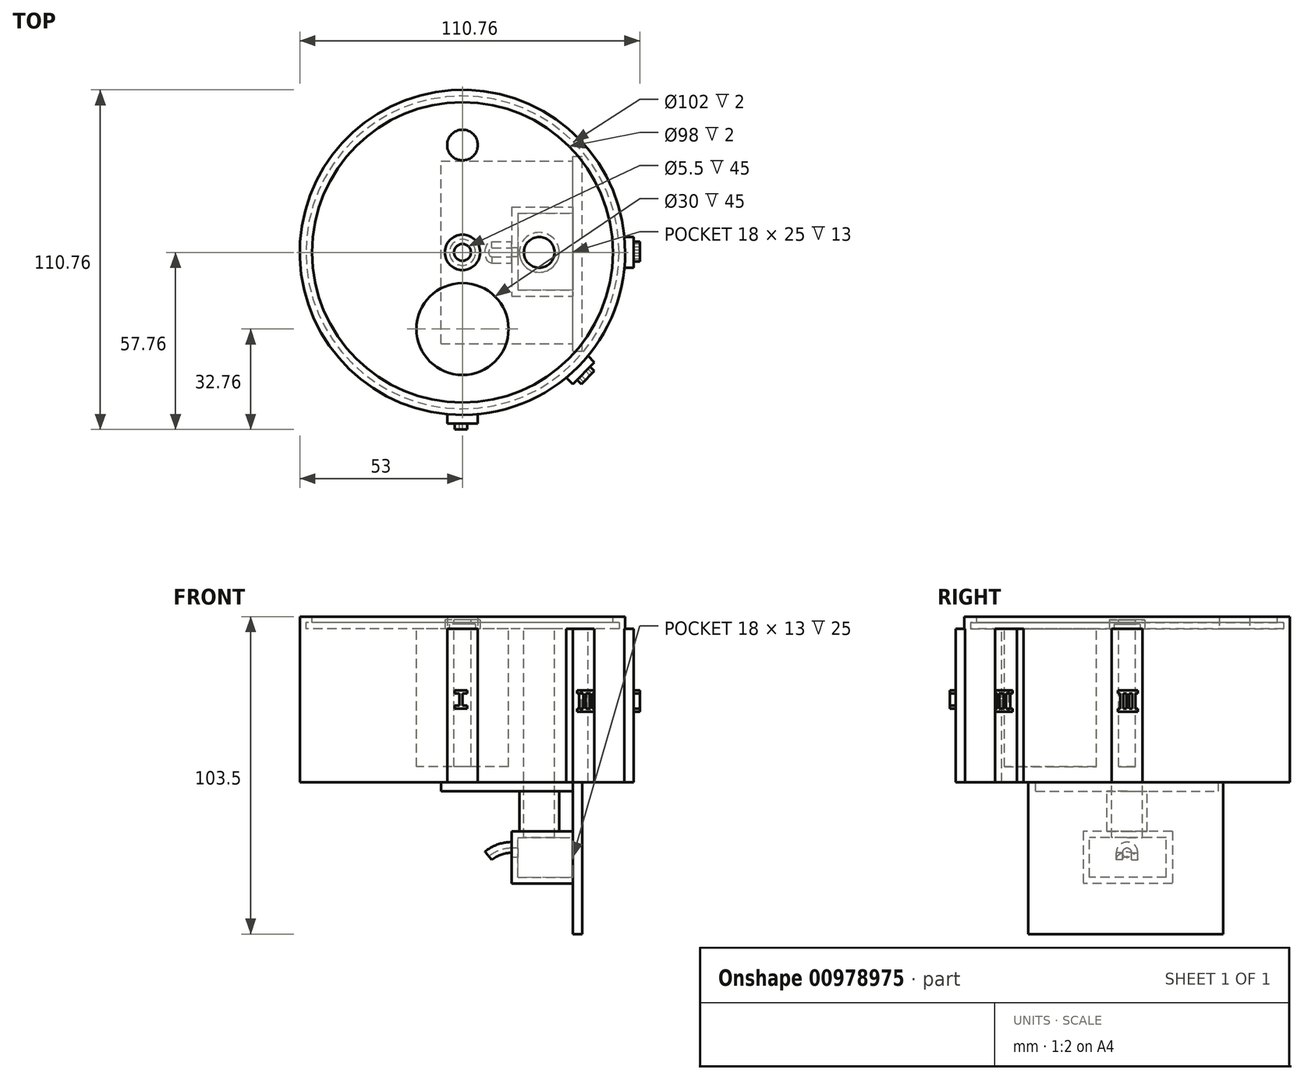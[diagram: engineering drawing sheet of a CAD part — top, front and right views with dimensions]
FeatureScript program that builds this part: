
annotation { "Feature Type Name" : "Feature", "Feature Type Description" : "" }
export const myFeature = defineFeature(function(context is Context, id is Id, definition is map)
    precondition{}
    {
        {
            var Q0;
            Q0=qCreatedBy(makeId("Top.planeOp"),FACE);
            var sketch = newSketch(context, id + "F0", { "sketchPlane" : qUnion([Q0])});
            skCircle(sketch, "E0", {"center": v(0, 0) * mm, "radius": 53 * mm});
            skSolve(sketch);
        }
        {
            var Q0;
            Q0=makeQuery(id+"F0.imprint","IMPRINT",FACE,{"disambiguationData":[TD([[makeQuery(id+"F0.imprint","IMPRINT",EDGE,{"derivedFrom":sQuery(id+"F0.wireOp",EDGE,"E0")}),1.0]])]});
            extrude(context, id + "F1", {"entities" : qUnion([Q0]), "depth" : 50 * mm, "offsetDistance" : 25 * mm});
        }
        {
            var Q0;
            Q0=makeQuery(id+"F1.opExtrude","CAP_FACE",FACE,{"disambiguationData":[OSD([sQuery(id+"F0.wireOp",EDGE,"E0")])],"isStart":false});
            var sketch = newSketch(context, id + "F2", { "sketchPlane" : qUnion([Q0])});
            skCircle(sketch, "E1", {"center": v(0, 0) * mm, "radius": 5.75 * mm});
            skCircle(sketch, "E2", {"center": v(0, 0) * mm, "radius": 51 * mm});
            skCircle(sketch, "E3", {"center": v(0, 0) * mm, "radius": 4.25 * mm});
            skCircle(sketch, "E4", {"center": v(0, 0) * mm, "radius": 2.75 * mm});
            skCircle(sketch, "E5", {"center": v(0, 35) * mm, "radius": 5 * mm});
            skCircle(sketch, "E6", {"center": v(0, -25) * mm, "radius": 15 * mm});
            skCircle(sketch, "E7", {"center": v(25, 0) * mm, "radius": 5 * mm});
            skLineSegment(sketch, "E8", {"start": v(-5, -52.76) * mm, "end": v(-5, -55.76) * mm});
            skLineSegment(sketch, "E9", {"start": v(-5, -55.76) * mm, "end": v(5, -55.76) * mm});
            skLineSegment(sketch, "E10", {"start": v(5, -55.76) * mm, "end": v(5, -52.76) * mm});
            skLineSegment(sketch, "E11", {"start": v(52.76, -5) * mm, "end": v(55.76, -5) * mm});
            skLineSegment(sketch, "E12", {"start": v(55.76, -5) * mm, "end": v(55.76, 5) * mm});
            skLineSegment(sketch, "E13", {"start": v(55.76, 5) * mm, "end": v(52.76, 5) * mm});
            skLineSegment(sketch, "E14", {"start": v(33.77, -40.85) * mm, "end": v(35.9, -42.97) * mm});
            skLineSegment(sketch, "E15", {"start": v(35.9, -42.97) * mm, "end": v(42.97, -35.9) * mm});
            skLineSegment(sketch, "E16", {"start": v(42.97, -35.9) * mm, "end": v(40.85, -33.77) * mm});
            skSolve(sketch);
        }
        {
            var Q0;
            Q0=makeQuery(id+"F2.imprint","IMPRINT",FACE,{"disambiguationData":[TD([[makeQuery(id+"F2.imprint","IMPRINT",EDGE,{"derivedFrom":sQuery(id+"F2.wireOp",EDGE,"E1")}),1.0]])]});
            extrude(context, id + "F3", {"entities" : qUnion([Q0]), "operationType" : NewBodyOperationType.ADD, "depth" : 3 * mm, "offsetDistance" : 25 * mm});
        }
        {
            var Q0;
            Q0=makeQuery(id+"F2.imprint","IMPRINT",FACE,{"disambiguationData":[TD([[makeQuery(id+"F2.imprint","IMPRINT",EDGE,{"derivedFrom":sQuery(id+"F2.wireOp",EDGE,"E2")}),-1.0]])]});
            extrude(context, id + "F4", {"entities" : qUnion([Q0]), "operationType" : NewBodyOperationType.ADD, "depth" : 4 * mm, "offsetDistance" : 25 * mm});
        }
        {
            var Q0;
            Q0=makeQuery(id+"F2.imprint","IMPRINT",FACE,{"disambiguationData":[TD([[makeQuery(id+"F2.imprint","IMPRINT",EDGE,{"derivedFrom":sQuery(id+"F2.wireOp",EDGE,"E4")}),1.0]])]});
            extrude(context, id + "F5", {"entities" : qUnion([Q0]), "operationType" : NewBodyOperationType.REMOVE, "oppositeDirection" : true, "depth" : 45 * mm, "offsetDistance" : 25 * mm});
        }
        {
            var Q0;
            Q0=makeQuery(id+"F4.opExtrude","CAP_FACE",FACE,{"disambiguationData":[OSD([sQuery(id+"F0.wireOp",EDGE,"E0"),sQuery(id+"F2.wireOp",EDGE,"E2")])],"isStart":false});
            var sketch = newSketch(context, id + "F6", { "sketchPlane" : qUnion([Q0])});
            skCircle(sketch, "E17", {"center": v(0, 0) * mm, "radius": 49 * mm});
            skSolve(sketch);
        }
        {
            var Q0;
            Q0=makeQuery(id+"F6.imprint","IMPRINT",FACE,{"disambiguationData":[TD([[makeQuery(id+"F6.imprint","IMPRINT",EDGE,{"derivedFrom":sQuery(id+"F6.wireOp",EDGE,"E17")}),-1.0]])]});
            extrude(context, id + "F7", {"entities" : qUnion([Q0]), "operationType" : NewBodyOperationType.ADD, "oppositeDirection" : true, "depth" : 2 * mm, "offsetDistance" : 25 * mm});
        }
        {
            var Q0;
            Q0=makeQuery(id+"F3.opExtrude","CAP_FACE",FACE,{"disambiguationData":[OSD([sQuery(id+"F2.wireOp",EDGE,"E1"),sQuery(id+"F2.wireOp",EDGE,"E3")])],"isStart":false});
            var sketch = newSketch(context, id + "F8", { "sketchPlane" : qUnion([Q0])});
            skCircle(sketch, "E18", {"center": v(0, 0) * mm, "radius": 2.75 * mm});
            skSolve(sketch);
        }
        {
            var Q0;
            Q0=makeQuery(id+"F8.imprint","IMPRINT",FACE,{"disambiguationData":[TD([[makeQuery(id+"F8.imprint","IMPRINT",EDGE,{"derivedFrom":sQuery(id+"F8.wireOp",EDGE,"E18")}),-1.0]])]});
            extrude(context, id + "F9", {"entities" : qUnion([Q0]), "operationType" : NewBodyOperationType.ADD, "oppositeDirection" : true, "depth" : 1.5 * mm, "offsetDistance" : 25 * mm});
        }
        {
            var Q0;
            Q0=makeQuery(id+"F2.imprint","IMPRINT",FACE,{"disambiguationData":[TD([[makeQuery(id+"F2.imprint","IMPRINT",EDGE,{"derivedFrom":sQuery(id+"F2.wireOp",EDGE,"E5")}),1.0]])]});
            extrude(context, id + "F10", {"entities" : qUnion([Q0]), "operationType" : NewBodyOperationType.ADD, "depth" : 4 * mm, "offsetDistance" : 25 * mm});
        }
        {
            var Q0;
            Q0=makeQuery(id+"F2.imprint","IMPRINT",FACE,{"disambiguationData":[TD([[makeQuery(id+"F2.imprint","IMPRINT",EDGE,{"derivedFrom":sQuery(id+"F2.wireOp",EDGE,"E7")}),1.0]])]});
            extrude(context, id + "F11", {"entities" : qUnion([Q0]), "operationType" : NewBodyOperationType.REMOVE, "oppositeDirection" : true, "depth" : 150 * mm, "offsetDistance" : 25 * mm});
        }
        {
            var Q0;
            Q0=makeQuery(id+"F2.imprint","IMPRINT",FACE,{"disambiguationData":[TD([[makeQuery(id+"F2.imprint","IMPRINT",EDGE,{"derivedFrom":sQuery(id+"F2.wireOp",EDGE,"E6")}),1.0]])]});
            extrude(context, id + "F12", {"entities" : qUnion([Q0]), "operationType" : NewBodyOperationType.REMOVE, "oppositeDirection" : true, "depth" : 45 * mm, "offsetDistance" : 25 * mm});
        }
        {
            var Q0;
            {var subQ0=sQuery(id+"F2.wireOp",EDGE,"E11");Q0=makeQuery(id+"F2.imprint","IMPRINT",FACE,{"disambiguationData":[TD([[makeQuery(id+"F2.imprint","IMPRINT",EDGE,{"derivedFrom":subQ0}),1.0]])]});}
            var Q1;
            {var subQ0=sQuery(id+"F2.wireOp",EDGE,"E8");Q1=makeQuery(id+"F2.imprint","IMPRINT",FACE,{"disambiguationData":[TD([[makeQuery(id+"F2.imprint","IMPRINT",EDGE,{"derivedFrom":subQ0}),1.0]])]});}
            var Q2;
            {var subQ0=sQuery(id+"F2.wireOp",EDGE,"E14");Q2=makeQuery(id+"F2.imprint","IMPRINT",FACE,{"disambiguationData":[TD([[makeQuery(id+"F2.imprint","IMPRINT",EDGE,{"derivedFrom":subQ0}),1.0]])]});}
            extrude(context, id + "F13", {"entities" : qUnion([Q0, Q1, Q2]), "operationType" : NewBodyOperationType.ADD, "oppositeDirection" : true, "depth" : 50 * mm, "offsetDistance" : 25 * mm});
        }
        {
            var Q0;
            {var subQ0=sQuery(id+"F0.wireOp",EDGE,"E0");Q0=makeQuery(id+"F13.boolean.opBoolean","MERGE",FACE,{"derivedFrom":[makeQuery(id+"F1.opExtrude","CAP_FACE",FACE,{"disambiguationData":[OSD([subQ0])],"isStart":true}),makeQuery(id+"F13.opExtrude","CAP_FACE",FACE,{"disambiguationData":[OSD([subQ0,sQuery(id+"F2.wireOp",EDGE,"E8"),sQuery(id+"F2.wireOp",EDGE,"E9"),sQuery(id+"F2.wireOp",EDGE,"E10")])],"isStart":false}),makeQuery(id+"F13.opExtrude","CAP_FACE",FACE,{"disambiguationData":[OSD([subQ0,sQuery(id+"F2.wireOp",EDGE,"E11"),sQuery(id+"F2.wireOp",EDGE,"E12"),sQuery(id+"F2.wireOp",EDGE,"E13")])],"isStart":false}),makeQuery(id+"F13.opExtrude","CAP_FACE",FACE,{"disambiguationData":[OSD([subQ0,sQuery(id+"F2.wireOp",EDGE,"E14"),sQuery(id+"F2.wireOp",EDGE,"E15"),sQuery(id+"F2.wireOp",EDGE,"E16")])],"isStart":false})]});}
            var sketch = newSketch(context, id + "F14", { "sketchPlane" : qUnion([Q0])});
            skLineSegment(sketch, "E19.bottom", {"start": v(-7, 29.75) * mm, "end": v(36, 29.75) * mm});
            skLineSegment(sketch, "E19.top", {"start": v(-7, -29.75) * mm, "end": v(36, -29.75) * mm});
            skLineSegment(sketch, "E19.left", {"start": v(-7, 29.75) * mm, "end": v(-7, -29.75) * mm});
            skLineSegment(sketch, "E19.right", {"start": v(36, 29.75) * mm, "end": v(36, -29.75) * mm});
            skLineSegment(sketch, "E20.bottom", {"start": v(36, 32.25) * mm, "end": v(39, 32.25) * mm});
            skLineSegment(sketch, "E20.top", {"start": v(36, -31.25) * mm, "end": v(39, -31.25) * mm});
            skLineSegment(sketch, "E20.left", {"start": v(36, 32.25) * mm, "end": v(36, -31.25) * mm});
            skLineSegment(sketch, "E20.right", {"start": v(39, 32.25) * mm, "end": v(39, -31.25) * mm});
            skSolve(sketch);
        }
        {
            var Q0;
            Q0=makeQuery(id+"F14.imprint","IMPRINT",FACE,{"disambiguationData":[TD([[makeQuery(id+"F14.imprint","IMPRINT",EDGE,{"derivedFrom":sQuery(id+"F14.wireOp",EDGE,"E19.bottom")}),-1.0]])]});
            extrude(context, id + "F15", {"entities" : qUnion([Q0]), "operationType" : NewBodyOperationType.ADD, "depth" : 3 * mm, "offsetDistance" : 25 * mm});
        }
        {
            var Q0;
            {var subQ1=sQuery(id+"F14.wireOp",EDGE,"E19.right");Q0=makeQuery(id+"F14.imprint","IMPRINT",FACE,{"disambiguationData":[TD([[makeQuery(id+"F14.imprint","IMPRINT",EDGE,{"derivedFrom":subQ1}),1.0]])]});}
            extrude(context, id + "F16", {"entities" : qUnion([Q0]), "operationType" : NewBodyOperationType.ADD, "depth" : 49.5 * mm, "offsetDistance" : 25 * mm});
        }
        {
            var Q0;
            Q0=makeQuery(id+"F15.opExtrude","CAP_FACE",FACE,{"disambiguationData":[OSD([sQuery(id+"F0.wireOp",EDGE,"E0"),sQuery(id+"F2.wireOp",EDGE,"E7"),sQuery(id+"F14.wireOp",EDGE,"E19.bottom"),sQuery(id+"F14.wireOp",EDGE,"E19.top"),sQuery(id+"F14.wireOp",EDGE,"E19.left"),sQuery(id+"F14.wireOp",EDGE,"E19.right")])],"isStart":false});
            var sketch = newSketch(context, id + "F17", { "sketchPlane" : qUnion([Q0])});
            skCircle(sketch, "E21", {"center": v(25, 0) * mm, "radius": 6.5 * mm});
            skSolve(sketch);
        }
        {
            var Q0;
            Q0=makeQuery(id+"F17.imprint","IMPRINT",FACE,{"disambiguationData":[TD([[makeQuery(id+"F17.imprint","IMPRINT",EDGE,{"derivedFrom":sQuery(id+"F17.wireOp",EDGE,"E21")}),1.0]])]});
            extrude(context, id + "F18", {"entities" : qUnion([Q0]), "operationType" : NewBodyOperationType.ADD, "depth" : 15 * mm, "offsetDistance" : 25 * mm});
        }
        {
            var Q0;
            Q0=makeQuery(id+"F16.opExtrude","SWEPT_FACE",FACE,{"disambiguationData":[OSD([sQuery(id+"F14.wireOp",EDGE,"E19.right"),sQuery(id+"F14.wireOp",EDGE,"E20.left")])]});
            var sketch = newSketch(context, id + "F19", { "sketchPlane" : qUnion([Q0])});
            skLineSegment(sketch, "E22.bottom", {"start": v(-14.75, -16) * mm, "end": v(14.25, -16) * mm});
            skLineSegment(sketch, "E22.top", {"start": v(-14.75, -33) * mm, "end": v(14.25, -33) * mm});
            skLineSegment(sketch, "E22.left", {"start": v(-14.75, -16) * mm, "end": v(-14.75, -33) * mm});
            skLineSegment(sketch, "E22.right", {"start": v(14.25, -16) * mm, "end": v(14.25, -33) * mm});
            skLineSegment(sketch, "E23.bottom", {"start": v(-12.75, -31) * mm, "end": v(12.25, -31) * mm});
            skLineSegment(sketch, "E23.top", {"start": v(-12.75, -18) * mm, "end": v(12.25, -18) * mm});
            skLineSegment(sketch, "E23.left", {"start": v(-12.75, -31) * mm, "end": v(-12.75, -18) * mm});
            skLineSegment(sketch, "E23.right", {"start": v(12.25, -31) * mm, "end": v(12.25, -18) * mm});
            skSolve(sketch);
        }
        {
            var Q0;
            Q0=makeQuery(id+"F19.imprint","IMPRINT",FACE,{"disambiguationData":[TD([[makeQuery(id+"F19.imprint","IMPRINT",EDGE,{"derivedFrom":sQuery(id+"F19.wireOp",EDGE,"E22.bottom")}),-1.0]])]});
            extrude(context, id + "F20", {"entities" : qUnion([Q0]), "operationType" : NewBodyOperationType.ADD, "depth" : 20 * mm, "offsetDistance" : 25 * mm});
        }
        {
            var Q0;
            Q0=makeQuery(id+"F20.boolean.opBoolean","MERGE",FACE,{"derivedFrom":[makeQuery(id+"F18.opExtrude","CAP_FACE",FACE,{"disambiguationData":[OSD([sQuery(id+"F0.wireOp",EDGE,"E0"),sQuery(id+"F2.wireOp",EDGE,"E7"),sQuery(id+"F17.wireOp",EDGE,"E21")])],"isStart":false}),makeQuery(id+"F20.opExtrude","SWEPT_FACE",FACE,{"disambiguationData":[OSD([sQuery(id+"F19.wireOp",EDGE,"E23.top")])]})]});
            var sketch = newSketch(context, id + "F21", { "sketchPlane" : qUnion([Q0])});
            skCircle(sketch, "E24", {"center": v(25, 0) * mm, "radius": 5 * mm});
            skSolve(sketch);
        }
        {
            var Q0;
            Q0=makeQuery(id+"F21.imprint","IMPRINT",FACE,{"disambiguationData":[TD([[makeQuery(id+"F21.imprint","IMPRINT",EDGE,{"derivedFrom":sQuery(id+"F21.wireOp",EDGE,"E24")}),1.0]])]});
            extrude(context, id + "F22", {"entities" : qUnion([Q0]), "operationType" : NewBodyOperationType.REMOVE, "oppositeDirection" : true, "depth" : 25 * mm, "offsetDistance" : 25 * mm});
        }
        {
            var Q0;
            Q0=makeQuery(id+"F20.opExtrude","CAP_FACE",FACE,{"disambiguationData":[OSD([sQuery(id+"F19.wireOp",EDGE,"E22.bottom"),sQuery(id+"F19.wireOp",EDGE,"E22.top"),sQuery(id+"F19.wireOp",EDGE,"E22.left"),sQuery(id+"F19.wireOp",EDGE,"E22.right"),sQuery(id+"F19.wireOp",EDGE,"E23.bottom"),sQuery(id+"F19.wireOp",EDGE,"E23.top"),sQuery(id+"F19.wireOp",EDGE,"E23.left"),sQuery(id+"F19.wireOp",EDGE,"E23.right")])],"isStart":false});
            var sketch = newSketch(context, id + "F23", { "sketchPlane" : qUnion([Q0])});
            skCircle(sketch, "E25", {"center": v(0, -23) * mm, "radius": 1.5 * mm});
            skCircle(sketch, "E26", {"center": v(0, -23) * mm, "radius": 3.5 * mm});
            skLineSegment(sketch, "E27", {"start": v(0, -23) * mm, "end": v(-3.5, -23) * mm});
            skLineSegment(sketch, "E28", {"start": v(-3.5, -23) * mm, "end": v(3.5, -23) * mm});
            skSolve(sketch);
        }
        {
            var Q0;
            Q0=makeQuery(id+"F23.imprint","IMPRINT",FACE,{"disambiguationData":[TD([[makeQuery(id+"F23.imprint","IMPRINT",EDGE,{"derivedFrom":makeQuery(id+"F20.opExtrude","CAP_EDGE",EDGE,{"disambiguationData":[OSD([sQuery(id+"F19.wireOp",EDGE,"E23.bottom")])],"isStart":false})}),1.0]])]});
            var Q1;
            {var subQ0=sQuery(id+"F23.wireOp",EDGE,"E27");var subQ1=sQuery(id+"F23.wireOp",EDGE,"E25");var subQ2=makeQuery(id+"F23.imprint","INTERSECT",VERTEX,{"derivedFrom":[subQ1,subQ0]});Q1=makeQuery(id+"F23.imprint","IMPRINT",FACE,{"disambiguationData":[TD([[makeQuery(id+"F23.imprint","IMPRINT",EDGE,{"disambiguationData":[TD([[subQ2,-1.0]])],"derivedFrom":subQ1}),-1.0]])]});}
            var Q2;
            {var subQ0=sQuery(id+"F23.wireOp",EDGE,"E27");var subQ1=sQuery(id+"F23.wireOp",EDGE,"E25");var subQ2=makeQuery(id+"F23.imprint","INTERSECT",VERTEX,{"derivedFrom":[subQ1,subQ0]});Q2=makeQuery(id+"F23.imprint","IMPRINT",FACE,{"disambiguationData":[TD([[makeQuery(id+"F23.imprint","IMPRINT",EDGE,{"disambiguationData":[TD([[subQ2,1.0]])],"derivedFrom":subQ1}),-1.0]])]});}
            extrude(context, id + "F24", {"entities" : qUnion([Q0, Q1, Q2]), "operationType" : NewBodyOperationType.ADD, "oppositeDirection" : true, "depth" : 2 * mm, "offsetDistance" : 25 * mm});
        }
        {
            var Q0;
            {var subQ0=sQuery(id+"F23.wireOp",EDGE,"E27");var subQ1=sQuery(id+"F23.wireOp",EDGE,"E25");var subQ2=makeQuery(id+"F23.imprint","INTERSECT",VERTEX,{"derivedFrom":[subQ1,subQ0]});Q0=makeQuery(id+"F23.imprint","IMPRINT",FACE,{"disambiguationData":[TD([[makeQuery(id+"F23.imprint","IMPRINT",EDGE,{"disambiguationData":[TD([[subQ2,1.0]])],"derivedFrom":subQ1}),-1.0]])]});}
            var Q1;
            Q1=makeQuery(id+"F20.opExtrude","CAP_EDGE",EDGE,{"disambiguationData":[OSD([sQuery(id+"F19.wireOp",EDGE,"E22.top")])],"isStart":false});
            revolve(context, id + "F25", {"operationType" : NewBodyOperationType.ADD, "surfaceOperationType" : NewSurfaceOperationType.NEW, "entities" : qUnion([Q0]), "axis" : qUnion([Q1]), "revolveType" : RevolveType.ONE_DIRECTION, "angle" : 40 * degree});
        }
        {
            var Q0;
            Q0=makeQuery(id+"F13.opExtrude","SWEPT_FACE",FACE,{"disambiguationData":[OSD([sQuery(id+"F2.wireOp",EDGE,"E9")])]});
            var sketch = newSketch(context, id + "F26", { "sketchPlane" : qUnion([Q0])});
            skLineSegment(sketch, "E29", {"start": v(-2.5, 30) * mm, "end": v(1.5, 30) * mm});
            skLineSegment(sketch, "E30", {"start": v(1.5, 30) * mm, "end": v(1.5, 29) * mm});
            skLineSegment(sketch, "E31", {"start": v(1.5, 29) * mm, "end": v(0, 29) * mm});
            skLineSegment(sketch, "E32", {"start": v(0, 29) * mm, "end": v(0, 25) * mm});
            skLineSegment(sketch, "E33", {"start": v(0, 25) * mm, "end": v(1.5, 25) * mm});
            skLineSegment(sketch, "E34", {"start": v(1.5, 25) * mm, "end": v(1.5, 24) * mm});
            skLineSegment(sketch, "E35", {"start": v(1.5, 24) * mm, "end": v(-2.5, 24) * mm});
            skLineSegment(sketch, "E36", {"start": v(-2.5, 24) * mm, "end": v(-2.5, 25) * mm});
            skLineSegment(sketch, "E37", {"start": v(-2.5, 25) * mm, "end": v(-1, 25) * mm});
            skLineSegment(sketch, "E38", {"start": v(-1, 25) * mm, "end": v(-1, 29) * mm});
            skLineSegment(sketch, "E39", {"start": v(-1, 29) * mm, "end": v(-2.5, 29) * mm});
            skLineSegment(sketch, "E40", {"start": v(-2.5, 29) * mm, "end": v(-2.5, 30) * mm});
            skSolve(sketch);
        }
        {
            var Q0;
            Q0=makeQuery(id+"F26.imprint","IMPRINT",FACE,{"disambiguationData":[TD([[makeQuery(id+"F26.imprint","IMPRINT",EDGE,{"derivedFrom":sQuery(id+"F26.wireOp",EDGE,"E29")}),-1.0]])]});
            extrude(context, id + "F27", {"entities" : qUnion([Q0]), "operationType" : NewBodyOperationType.ADD, "depth" : 2 * mm, "offsetDistance" : 25 * mm});
        }
        {
            var Q0;
            Q0=makeQuery(id+"F13.opExtrude","SWEPT_FACE",FACE,{"disambiguationData":[OSD([sQuery(id+"F2.wireOp",EDGE,"E15")])]});
            var sketch = newSketch(context, id + "F28", { "sketchPlane" : qUnion([Q0])});
            skLineSegment(sketch, "E41", {"start": v(-3, 30) * mm, "end": v(3, 30) * mm});
            skLineSegment(sketch, "E42", {"start": v(3, 30) * mm, "end": v(3, 29) * mm});
            skLineSegment(sketch, "E43", {"start": v(3, 29) * mm, "end": v(2, 29) * mm});
            skLineSegment(sketch, "E44", {"start": v(2, 29) * mm, "end": v(2, 24) * mm});
            skLineSegment(sketch, "E45", {"start": v(2, 24) * mm, "end": v(3, 24) * mm});
            skLineSegment(sketch, "E46", {"start": v(3, 24) * mm, "end": v(3, 23) * mm});
            skLineSegment(sketch, "E47", {"start": v(3, 23) * mm, "end": v(-3, 23) * mm});
            skLineSegment(sketch, "E48", {"start": v(-3, 23) * mm, "end": v(-3, 24) * mm});
            skLineSegment(sketch, "E49", {"start": v(-3, 24) * mm, "end": v(-2, 24) * mm});
            skLineSegment(sketch, "E50", {"start": v(-2, 24) * mm, "end": v(-2, 29) * mm});
            skLineSegment(sketch, "E51", {"start": v(-2, 29) * mm, "end": v(-3, 29) * mm});
            skLineSegment(sketch, "E52", {"start": v(-3, 29) * mm, "end": v(-3, 30) * mm});
            skLineSegment(sketch, "E53", {"start": v(-1, 29) * mm, "end": v(1, 29) * mm});
            skLineSegment(sketch, "E54", {"start": v(1, 29) * mm, "end": v(1, 24) * mm});
            skLineSegment(sketch, "E55", {"start": v(1, 24) * mm, "end": v(-1, 24) * mm});
            skLineSegment(sketch, "E56", {"start": v(-1, 24) * mm, "end": v(-1, 29) * mm});
            skSolve(sketch);
        }
        {
            var Q0;
            Q0=makeQuery(id+"F28.imprint","IMPRINT",FACE,{"disambiguationData":[TD([[makeQuery(id+"F28.imprint","IMPRINT",EDGE,{"derivedFrom":sQuery(id+"F28.wireOp",EDGE,"E41")}),-1.0]])]});
            extrude(context, id + "F29", {"entities" : qUnion([Q0]), "operationType" : NewBodyOperationType.ADD, "depth" : 2 * mm, "offsetDistance" : 25 * mm});
        }
        {
            var Q0;
            Q0=makeQuery(id+"F13.opExtrude","SWEPT_FACE",FACE,{"disambiguationData":[OSD([sQuery(id+"F2.wireOp",EDGE,"E12")])]});
            var sketch = newSketch(context, id + "F30", { "sketchPlane" : qUnion([Q0])});
            skLineSegment(sketch, "E57", {"start": v(-3, 30) * mm, "end": v(3.5, 30) * mm});
            skLineSegment(sketch, "E58", {"start": v(3.5, 30) * mm, "end": v(3.5, 29) * mm});
            skLineSegment(sketch, "E59", {"start": v(3.5, 29) * mm, "end": v(2.75, 29) * mm});
            skLineSegment(sketch, "E60", {"start": v(2.75, 29) * mm, "end": v(2.75, 24) * mm});
            skLineSegment(sketch, "E61", {"start": v(2.75, 24) * mm, "end": v(3.5, 24) * mm});
            skLineSegment(sketch, "E62", {"start": v(3.5, 24) * mm, "end": v(3.5, 23) * mm});
            skLineSegment(sketch, "E63", {"start": v(3.5, 23) * mm, "end": v(-3, 23) * mm});
            skLineSegment(sketch, "E64", {"start": v(-3, 23) * mm, "end": v(-3, 24) * mm});
            skLineSegment(sketch, "E65", {"start": v(-3, 24) * mm, "end": v(-2.25, 24) * mm});
            skLineSegment(sketch, "E66", {"start": v(-2.25, 24) * mm, "end": v(-2.25, 29) * mm});
            skLineSegment(sketch, "E67", {"start": v(-2.25, 29) * mm, "end": v(-3, 29) * mm});
            skLineSegment(sketch, "E68", {"start": v(-3, 29) * mm, "end": v(-3, 30) * mm});
            skLineSegment(sketch, "E69", {"start": v(-1.25, 24) * mm, "end": v(-1.25, 29) * mm});
            skLineSegment(sketch, "E70", {"start": v(-1.25, 29) * mm, "end": v(-0.25, 29) * mm});
            skLineSegment(sketch, "E71", {"start": v(-0.25, 29) * mm, "end": v(-0.25, 24) * mm});
            skLineSegment(sketch, "E72", {"start": v(-0.25, 24) * mm, "end": v(-1.25, 24) * mm});
            skLineSegment(sketch, "E73", {"start": v(0.75, 24) * mm, "end": v(0.75, 29) * mm});
            skLineSegment(sketch, "E74", {"start": v(0.75, 29) * mm, "end": v(1.75, 29) * mm});
            skLineSegment(sketch, "E75", {"start": v(1.75, 29) * mm, "end": v(1.75, 24) * mm});
            skLineSegment(sketch, "E76", {"start": v(1.75, 24) * mm, "end": v(0.75, 24) * mm});
            skSolve(sketch);
        }
        {
            var Q0;
            Q0=makeQuery(id+"F30.imprint","IMPRINT",FACE,{"disambiguationData":[TD([[makeQuery(id+"F30.imprint","IMPRINT",EDGE,{"derivedFrom":sQuery(id+"F30.wireOp",EDGE,"E57")}),-1.0]])]});
            extrude(context, id + "F31", {"entities" : qUnion([Q0]), "operationType" : NewBodyOperationType.ADD, "depth" : 2 * mm, "offsetDistance" : 25 * mm});
        }
    });
